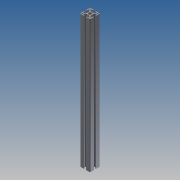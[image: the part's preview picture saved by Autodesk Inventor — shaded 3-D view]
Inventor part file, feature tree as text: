
AUTODESK INVENTOR PART (.ipt)
format: ipt  version: 2016 (Build 200138000, 138)  size: 215,552 bytes
history: native  units: mm
features: other x42, sketch x5, hole x4, extrude x1
ambient origin geometry x8: Origin, YZ Plane, XZ Plane, XY Plane, X Axis, Y Axis, Z Axis, Center Point
bodies: Solid1 (feature_tree)
feature tree (52):
  extrude  "Extrusion1"  [1 undecoded]
  hole  "Drilling 1"  [1 undecoded]
  hole  "Drilling 2"  [1 undecoded]
  hole  "Drilling 3"  [1 undecoded]
  hole  "Drilling 4"  [1 undecoded]
  other  "side_4d_XY"
  other  "side_4d_YZ"
  other  "side_4d_ZX"
  other  "side_4d_X"
  other  "side_4d_Y"
  other  "side_4d_Z"
  other  "side_4d_Center"
  other  "side_1a_XY"
  other  "side_1a_YZ"
  other  "side_1a_ZX"
  other  "side_1a_X"
  other  "side_1a_Y"
  other  "side_1a_Z"
  other  "side_1a_Center"
  other  "side_2b_XY"
  other  "side_2b_YZ"
  other  "side_2b_ZX"
  other  "side_2b_X"
  other  "side_2b_Y"
  other  "side_2b_Z"
  other  "side_2b_Center"
  other  "side_3c_XY"
  other  "side_3c_YZ"
  other  "side_3c_ZX"
  other  "side_3c_X"
  other  "side_3c_Y"
  other  "side_3c_Z"
  other  "side_3c_Center"
  other  "end_XY"
  other  "end_YZ"
  other  "end_ZX"
  other  "end_X"
  other  "end_Y"
  other  "end_Z"
  other  "end_Center"
  other  "start_XY"
  other  "start_YZ"
  other  "start_ZX"
  other  "start_X"
  other  "start_Y"
  other  "start_Z"
  other  "start_Center"
  sketch  "Skizze_1"  dims[d0=529.8mm d1=0.0mm]
  sketch  "Sketch2"  dims[d2=5.0mm d3=6.0mm d4=4.0mm d5=2.0mm d6=90.0deg d7=6000.0mm d8=0.0mm]
  sketch  "Sketch3"  dims[d9=5.0mm d10=6.0mm d11=4.0mm d12=2.0mm d13=90.0deg d14=6000.0mm d15=0.0mm]
  sketch  "Sketch4"  dims[d16=5.0mm d17=6.0mm d18=4.0mm d19=2.0mm d20=90.0deg d21=6000.0mm d22=0.0mm]
  sketch  "Sketch5"  dims[d23=5.0mm d24=6.0mm d25=4.0mm d26=2.0mm d27=90.0deg d28=6000.0mm d29=0.0mm]
note: 5 required parameter values undecoded (feature->parameter linkage not recoverable at this tier; creation-order binding heuristic only, values carry confidence <= 0.55)
